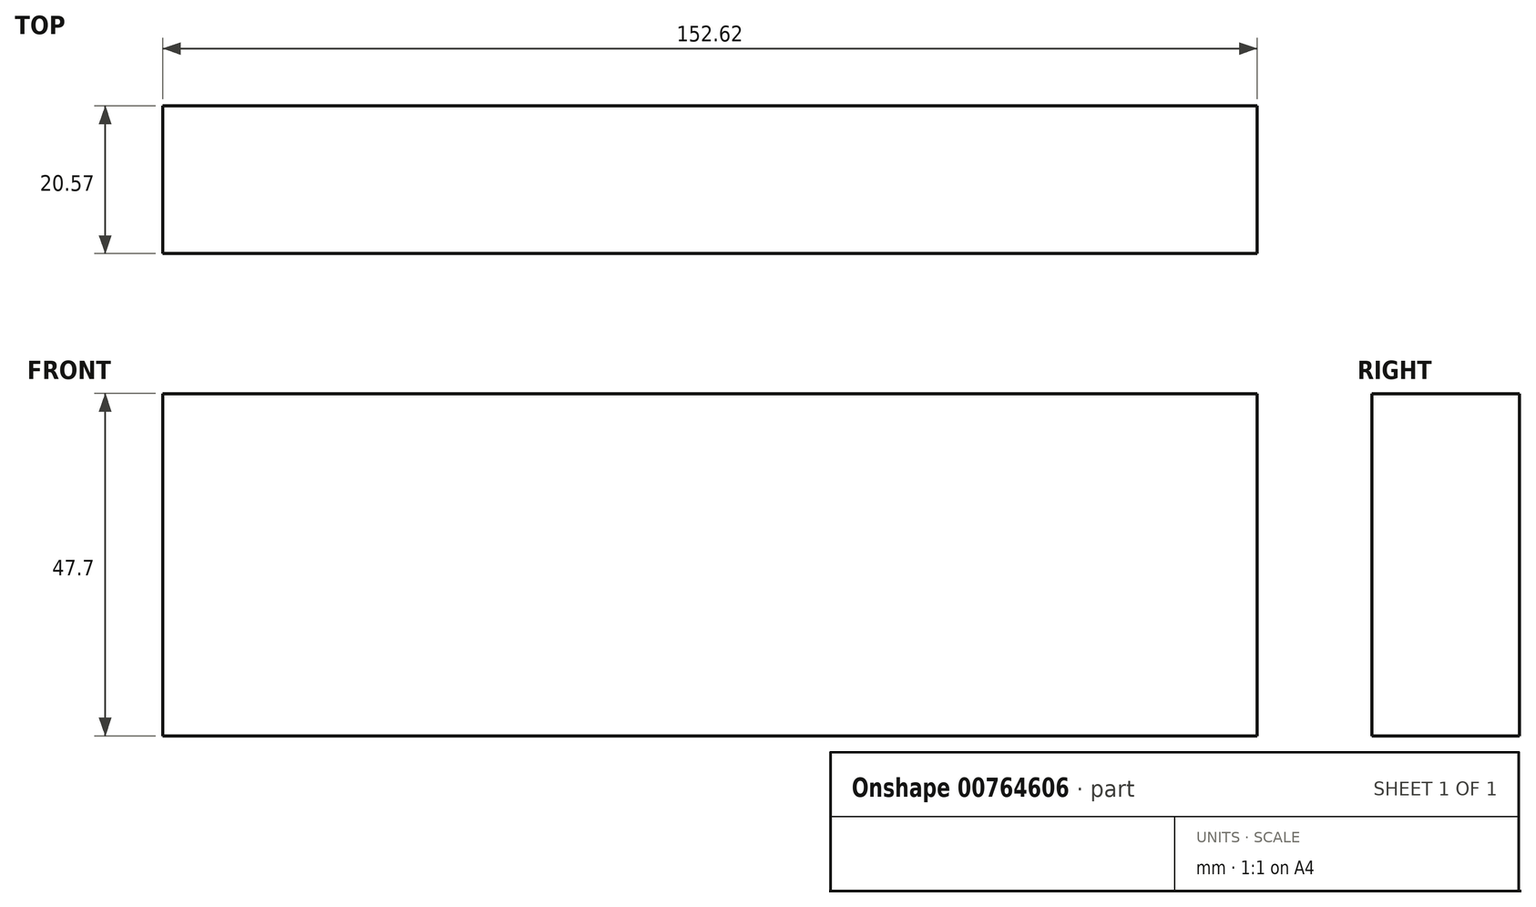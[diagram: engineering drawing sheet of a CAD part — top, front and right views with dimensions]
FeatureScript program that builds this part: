
annotation { "Feature Type Name" : "Feature", "Feature Type Description" : "" }
export const myFeature = defineFeature(function(context is Context, id is Id, definition is map)
    precondition{}
    {
        {
            var Q0;
            Q0=qCreatedBy(makeId("Front.planeOp"),FACE);
            var sketch = newSketch(context, id + "F0", { "sketchPlane" : qUnion([Q0])});
            skLineSegment(sketch, "E0.bottom", {"start": v(-76.4, -28.32) * mm, "end": v(76.21, -28.32) * mm});
            skLineSegment(sketch, "E0.top", {"start": v(-76.4, -76.02) * mm, "end": v(76.21, -76.02) * mm});
            skLineSegment(sketch, "E0.left", {"start": v(-76.4, -28.32) * mm, "end": v(-76.4, -76.02) * mm});
            skLineSegment(sketch, "E0.right", {"start": v(76.21, -28.32) * mm, "end": v(76.21, -76.02) * mm});
            skSolve(sketch);
        }
        {
            var Q0;
            Q0=makeQuery(id+"F0.imprint","IMPRINT",FACE,{"disambiguationData":[TD([[makeQuery(id+"F0.imprint","IMPRINT",EDGE,{"derivedFrom":sQuery(id+"F0.wireOp",EDGE,"E0.bottom")}),-1.0]])]});
            extrude(context, id + "F1", {"entities" : qUnion([Q0]), "depth" : 20.57 * mm, "offsetDistance" : 25.4 * mm});
        }
    });
